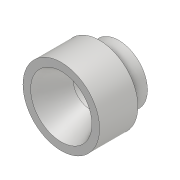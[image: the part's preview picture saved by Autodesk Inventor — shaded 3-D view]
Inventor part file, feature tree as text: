
AUTODESK INVENTOR PART (.ipt)
format: ipt  version: 2018.1 (Build 221171000, 171)  size: 114,176 bytes
history: native  units: mm
features: other x1, revolve x1, chamfer x1, sketch x1
ambient origin geometry x8: Origin, YZ Plane, XZ Plane, XY Plane, X Axis, Y Axis, Z Axis, Center Point
bodies: Body1 (feature_tree)
feature tree (4):
  other  "Твердое тело1"
  revolve  "Вращение1"
  chamfer  "Фаска1"  Distance=6.0mm
  sketch  "Эскиз1"
